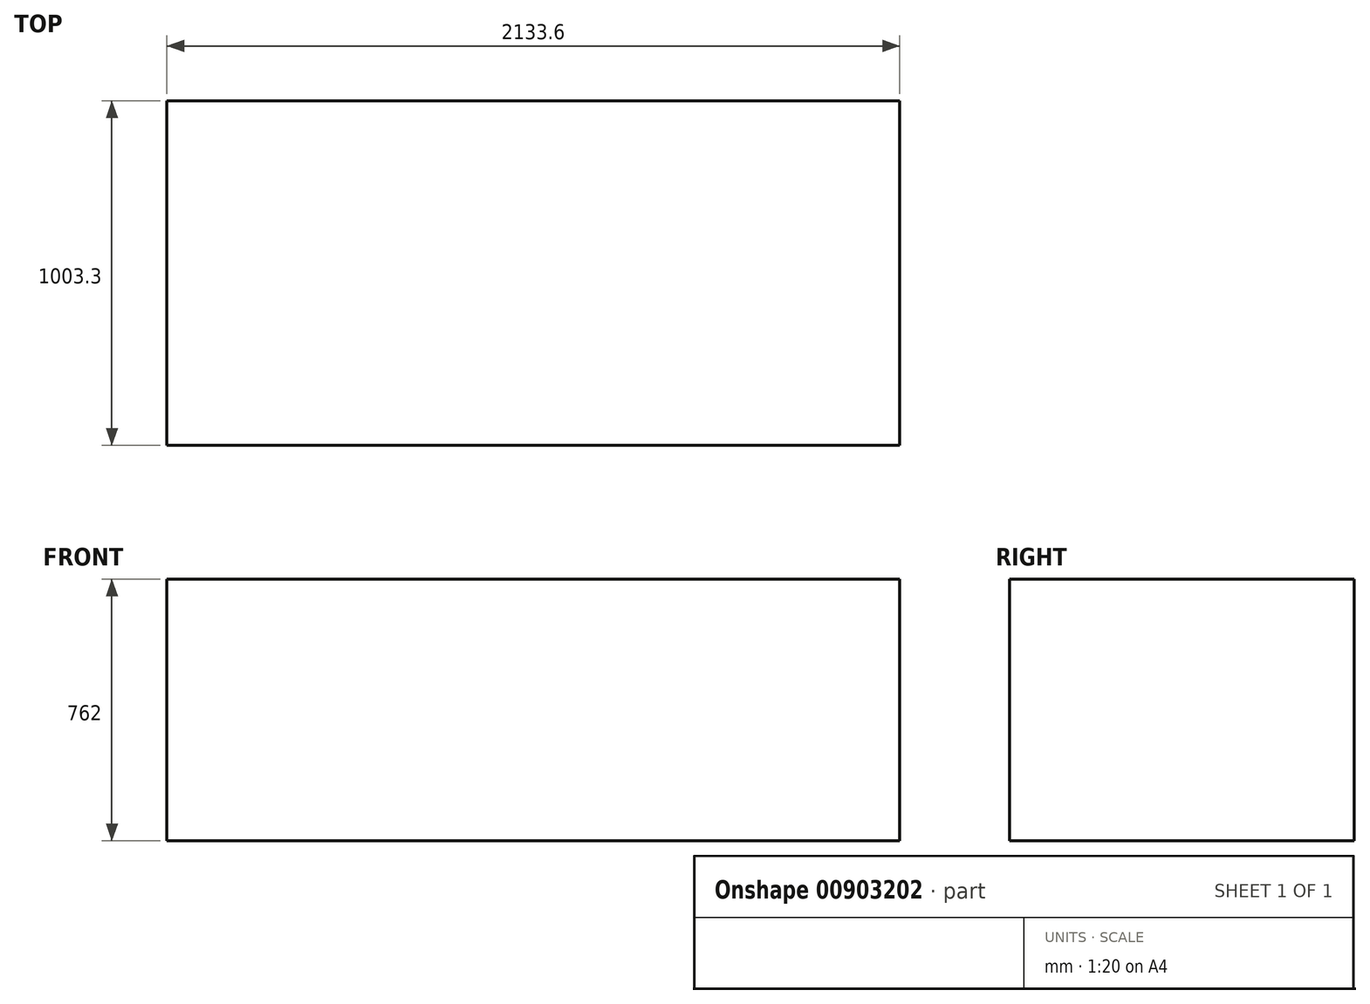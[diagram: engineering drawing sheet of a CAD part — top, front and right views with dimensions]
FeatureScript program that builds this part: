
annotation { "Feature Type Name" : "Feature", "Feature Type Description" : "" }
export const myFeature = defineFeature(function(context is Context, id is Id, definition is map)
    precondition{}
    {
        {
            var Q0;
            Q0=qCreatedBy(makeId("Top.planeOp"),FACE);
            var sketch = newSketch(context, id + "F0", { "sketchPlane" : qUnion([Q0])});
            skLineSegment(sketch, "E0.bottom", {"start": v(1066.8, 501.65) * mm, "end": v(-1066.8, 501.65) * mm});
            skLineSegment(sketch, "E0.top", {"start": v(1066.8, -501.65) * mm, "end": v(-1066.8, -501.65) * mm});
            skLineSegment(sketch, "E0.left", {"start": v(1066.8, 501.65) * mm, "end": v(1066.8, -501.65) * mm});
            skLineSegment(sketch, "E0.right", {"start": v(-1066.8, 501.65) * mm, "end": v(-1066.8, -501.65) * mm});
            skPoint(sketch, "E0.middle", {"position": v(0, 0) * mm});
            skSolve(sketch);
        }
        {
            var Q0;
            Q0=makeQuery(id+"F0.imprint","IMPRINT",FACE,{"disambiguationData":[TD([[makeQuery(id+"F0.imprint","IMPRINT",EDGE,{"derivedFrom":sQuery(id+"F0.wireOp",EDGE,"E0.bottom")}),1.0]])]});
            extrude(context, id + "F1", {"entities" : qUnion([Q0]), "depth" : 762 * mm, "offsetDistance" : 25.4 * mm});
        }
    });
